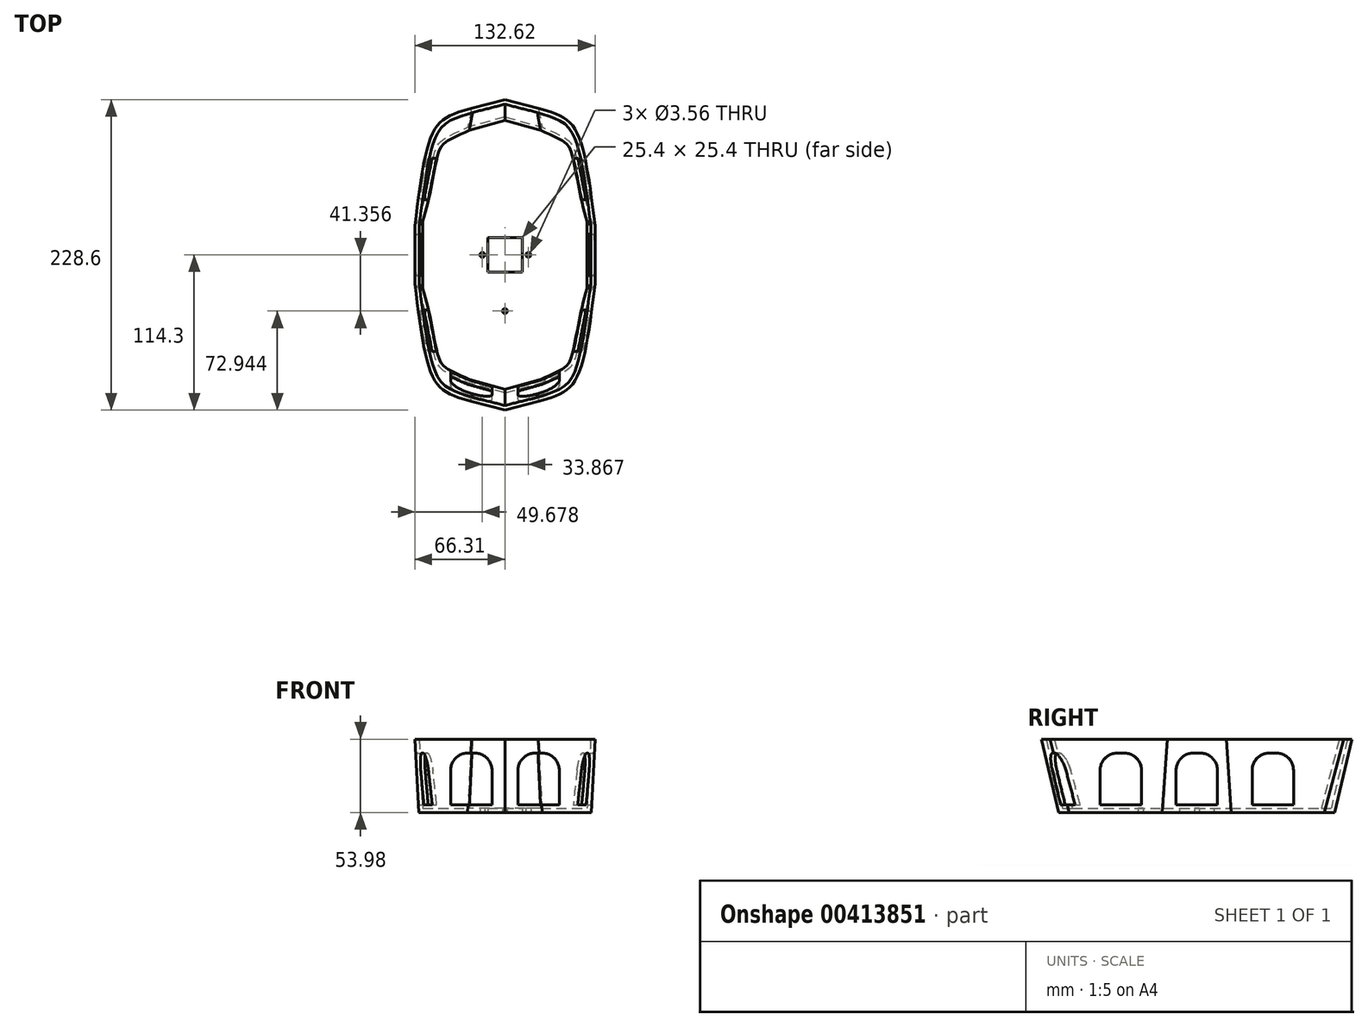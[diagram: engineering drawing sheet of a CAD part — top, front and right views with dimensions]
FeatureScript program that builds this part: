
annotation { "Feature Type Name" : "Feature", "Feature Type Description" : "" }
export const myFeature = defineFeature(function(context is Context, id is Id, definition is map)
    precondition{}
    {
        {
            var Q0;
            Q0=qCreatedBy(makeId("Top.planeOp"),FACE);
            var sketch = newSketch(context, id + "F0", { "sketchPlane" : qUnion([Q0])});
            skLineSegment(sketch, "E0", {"start": v(-63.5, 0) * mm, "end": v(-63.5, -25.4) * mm});
            skLineSegment(sketch, "E1", {"start": v(0, -101.6) * mm, "end": v(-27.43, -93.95) * mm});
            skFitSpline(sketch, "E2", {"points": [v(-63.5, -25.4) * mm, v(-51.66, -76.12) * mm, v(-27.43, -93.95) * mm], "startDerivative": vector(34.98, -106.28) * mm, "endDerivative": vector(126.69, -55.22) * mm});
            skFitSpline(sketch, "E3.MirrorCS", {"points": [v(-63.5, 25.4) * mm, v(-51.66, 76.12) * mm, v(-27.43, 93.95) * mm], "startDerivative": vector(34.98, 106.28) * mm, "endDerivative": vector(126.69, 55.22) * mm});
            skLineSegment(sketch, "E4.MirrorCS", {"start": v(0, 101.6) * mm, "end": v(-27.43, 93.95) * mm});
            skLineSegment(sketch, "E5.MirrorCS", {"start": v(-63.5, 0) * mm, "end": v(-63.5, 25.4) * mm});
            skLineSegment(sketch, "E6.MirrorCS", {"start": v(0, -101.6) * mm, "end": v(27.43, -93.95) * mm});
            skFitSpline(sketch, "E7.MirrorCS", {"points": [v(63.5, 25.4) * mm, v(51.66, 76.12) * mm, v(27.43, 93.95) * mm], "startDerivative": vector(-34.98, 106.28) * mm, "endDerivative": vector(-126.69, 55.22) * mm});
            skLineSegment(sketch, "E8.MirrorCS", {"start": v(63.5, 0) * mm, "end": v(63.5, -25.4) * mm});
            skFitSpline(sketch, "E9.MirrorCS", {"points": [v(63.5, -25.4) * mm, v(51.66, -76.12) * mm, v(27.43, -93.95) * mm], "startDerivative": vector(-34.98, -106.28) * mm, "endDerivative": vector(-126.69, -55.22) * mm});
            skLineSegment(sketch, "E10.MirrorCS", {"start": v(0, 101.6) * mm, "end": v(27.43, 93.95) * mm});
            skLineSegment(sketch, "E11.MirrorCS", {"start": v(63.5, 0) * mm, "end": v(63.5, 25.4) * mm});
            skLineSegment(sketch, "E12", {"start": v(63.5, 0) * mm, "end": v(-63.5, 0) * mm});
            skLineSegment(sketch, "E13", {"start": v(0, 101.6) * mm, "end": v(0, -101.6) * mm});
            skSolve(sketch);
        }
        {
            var Q0;
            Q0=qCreatedBy(makeId("Top.planeOp"),FACE);
            cPlane(context, id + "F1", {"entities" : qUnion([Q0]), "cplaneType" : CPlaneType.OFFSET, "offset" : 25.4 * mm, "oppositeDirection" : true, "width" : 152.4 * mm, "height" : 152.4 * mm});
        }
        {
            var Q0;
            Q0=qCreatedBy(makeId("Top.planeOp"),FACE);
            cPlane(context, id + "F2", {"entities" : qUnion([Q0]), "cplaneType" : CPlaneType.OFFSET, "offset" : 53.97 * mm, "width" : 152.4 * mm, "height" : 152.4 * mm});
        }
        {
            var Q0;
            Q0=qCreatedBy(id+"F2.planeOp",FACE);
            var sketch = newSketch(context, id + "F3", { "sketchPlane" : qUnion([Q0])});
            skLineSegment(sketch, "E14", {"start": v(0, 0) * mm, "end": v(0, -114.3) * mm});
            skLineSegment(sketch, "E15", {"start": v(0, 0) * mm, "end": v(66.31, 0) * mm});
            skLineSegment(sketch, "E16", {"start": v(66.31, 0) * mm, "end": v(66.31, -21.67) * mm});
            skLineSegment(sketch, "E17", {"start": v(0, -114.3) * mm, "end": v(24.62, -108.08) * mm});
            skFitSpline(sketch, "E18", {"points": [v(24.62, -108.08) * mm, v(43.46, -100.81) * mm, v(54.7, -86.27) * mm, v(66.31, -21.67) * mm], "startDerivative": vector(76.94, 22.9) * mm, "endDerivative": vector(19.57, 158.53) * mm});
            skLineSegment(sketch, "E19.MirrorCS", {"start": v(66.31, 0) * mm, "end": v(66.31, 21.67) * mm});
            skFitSpline(sketch, "E20.MirrorCS", {"points": [v(24.62, 108.08) * mm, v(43.46, 100.81) * mm, v(54.7, 86.27) * mm, v(66.31, 21.67) * mm], "startDerivative": vector(76.94, -22.9) * mm, "endDerivative": vector(19.57, -158.53) * mm});
            skLineSegment(sketch, "E21.MirrorCS", {"start": v(0, 114.3) * mm, "end": v(24.62, 108.08) * mm});
            skLineSegment(sketch, "E22.MirrorCS", {"start": v(0, 114.3) * mm, "end": v(-24.62, 108.08) * mm});
            skFitSpline(sketch, "E23.MirrorCS", {"points": [v(-24.62, 108.08) * mm, v(-43.46, 100.81) * mm, v(-54.7, 86.27) * mm, v(-66.31, 21.67) * mm], "startDerivative": vector(-76.94, -22.9) * mm, "endDerivative": vector(-19.57, -158.53) * mm});
            skLineSegment(sketch, "E24.MirrorCS", {"start": v(-66.31, 0) * mm, "end": v(-66.31, 21.67) * mm});
            skLineSegment(sketch, "E25.MirrorCS", {"start": v(-66.31, 0) * mm, "end": v(-66.31, -21.67) * mm});
            skFitSpline(sketch, "E26.MirrorCS", {"points": [v(-24.62, -108.08) * mm, v(-43.46, -100.81) * mm, v(-54.7, -86.27) * mm, v(-66.31, -21.67) * mm], "startDerivative": vector(-76.94, 22.9) * mm, "endDerivative": vector(-19.57, 158.53) * mm});
            skLineSegment(sketch, "E27.MirrorCS", {"start": v(0, -114.3) * mm, "end": v(-24.62, -108.08) * mm});
            skLineSegment(sketch, "E28", {"start": v(0, 114.3) * mm, "end": v(0, 0) * mm});
            skLineSegment(sketch, "E29", {"start": v(-66.31, 0) * mm, "end": v(0, 0) * mm});
            skSolve(sketch);
        }
        {
            var Q0;
            Q0=makeQuery(id+"F3.imprint","IMPRINT",FACE,{"disambiguationData":[TD([[makeQuery(id+"F3.imprint","IMPRINT",EDGE,{"derivedFrom":sQuery(id+"F3.wireOp",EDGE,"E22.MirrorCS")}),1.0]])]});
            var Q1;
            Q1=makeQuery(id+"F0.imprint","IMPRINT",FACE,{"disambiguationData":[TD([[makeQuery(id+"F0.imprint","IMPRINT",EDGE,{"derivedFrom":sQuery(id+"F0.wireOp",EDGE,"E3.MirrorCS")}),-1.0]])]});
            loft(context, id + "F4", {"sheetProfilesArray" : [{ "sheetProfileEntities" : qUnion([Q0]) }, { "sheetProfileEntities" : qUnion([Q1]) }]});
        }
        {
            var Q1;
            Q1=makeQuery(id+"F3.imprint","IMPRINT",FACE,{"disambiguationData":[TD([[makeQuery(id+"F3.imprint","IMPRINT",EDGE,{"derivedFrom":sQuery(id+"F3.wireOp",EDGE,"E14")}),-1.0]])]});
            var Q2;
            {var subQ1=sQuery(id+"F0.wireOp",EDGE,"E0");Q2=makeQuery(id+"F0.imprint","IMPRINT",FACE,{"disambiguationData":[TD([[makeQuery(id+"F0.imprint","IMPRINT",EDGE,{"derivedFrom":subQ1}),1.0]])]});}
            loft(context, id + "F5", {"operationType" : NewBodyOperationType.ADD, "sheetProfilesArray" : [{ "sheetProfileEntities" : qUnion([Q1]) }, { "sheetProfileEntities" : qUnion([Q2]) }]});
        }
        {
            var Q1;
            Q1=makeQuery(id+"F3.imprint","IMPRINT",FACE,{"disambiguationData":[TD([[makeQuery(id+"F3.imprint","IMPRINT",EDGE,{"derivedFrom":sQuery(id+"F3.wireOp",EDGE,"E14")}),1.0]])]});
            var Q2;
            {var subQ4=sQuery(id+"F0.wireOp",EDGE,"E6.MirrorCS");Q2=makeQuery(id+"F0.imprint","IMPRINT",FACE,{"disambiguationData":[TD([[makeQuery(id+"F0.imprint","IMPRINT",EDGE,{"derivedFrom":subQ4}),1.0]])]});}
            loft(context, id + "F6", {"operationType" : NewBodyOperationType.ADD, "sheetProfilesArray" : [{ "sheetProfileEntities" : qUnion([Q1]) }, { "sheetProfileEntities" : qUnion([Q2]) }]});
        }
        {
            var Q1;
            Q1=makeQuery(id+"F3.imprint","IMPRINT",FACE,{"disambiguationData":[TD([[makeQuery(id+"F3.imprint","IMPRINT",EDGE,{"derivedFrom":sQuery(id+"F3.wireOp",EDGE,"E15")}),1.0]])]});
            var Q2;
            Q2=makeQuery(id+"F0.imprint","IMPRINT",FACE,{"disambiguationData":[TD([[makeQuery(id+"F0.imprint","IMPRINT",EDGE,{"derivedFrom":sQuery(id+"F0.wireOp",EDGE,"E7.MirrorCS")}),1.0]])]});
            loft(context, id + "F7", {"operationType" : NewBodyOperationType.ADD, "sheetProfilesArray" : [{ "sheetProfileEntities" : qUnion([Q1]) }, { "sheetProfileEntities" : qUnion([Q2]) }]});
        }
        {
            var Q0;
            {var subQ0=makeQuery(id+"F3.imprint","IMPRINT",EDGE,{"derivedFrom":sQuery(id+"F3.wireOp",EDGE,"E15")});var subQ2=makeQuery(id+"F3.imprint","IMPRINT",EDGE,{"derivedFrom":sQuery(id+"F3.wireOp",EDGE,"E14")});Q0=makeQuery(id+"F7.boolean.opBoolean","MERGE",FACE,{"derivedFrom":[makeQuery(id+"F6.boolean.opBoolean","MERGE",FACE,{"derivedFrom":[makeQuery(id+"F5.boolean.opBoolean","MERGE",FACE,{"derivedFrom":[makeQuery(id+"F4.opLoft","CAP_FACE",FACE,{"disambiguationData":[OSD([makeQuery(id+"F3.imprint","IMPRINT",FACE,{"disambiguationData":[TD([[makeQuery(id+"F3.imprint","IMPRINT",EDGE,{"derivedFrom":sQuery(id+"F3.wireOp",EDGE,"E22.MirrorCS")}),1.0]])]})])],"isStart":true}),makeQuery(id+"F5.opLoft","CAP_FACE",FACE,{"disambiguationData":[OSD([makeQuery(id+"F3.imprint","IMPRINT",FACE,{"disambiguationData":[TD([[subQ2,-1.0]])]})])],"isStart":true})]}),makeQuery(id+"F6.opLoft","CAP_FACE",FACE,{"disambiguationData":[OSD([makeQuery(id+"F3.imprint","IMPRINT",FACE,{"disambiguationData":[TD([[subQ2,1.0]])]})])],"isStart":true})]}),makeQuery(id+"F7.opLoft","CAP_FACE",FACE,{"disambiguationData":[OSD([makeQuery(id+"F3.imprint","IMPRINT",FACE,{"disambiguationData":[TD([[subQ0,1.0]])]})])],"isStart":true})]});}
            shell(context, id + "F8", {"entities" : qUnion([Q0]), "thickness" : 3.17 * mm});
        }
        {
            var Q0;
            Q0=qCreatedBy(id+"F1.planeOp",FACE);
            var sketch = newSketch(context, id + "F9", { "sketchPlane" : qUnion([Q0])});
            skCircle(sketch, "E30", {"center": v(0, -41.36) * mm, "radius": 1.78 * mm});
            skLineSegment(sketch, "E31", {"start": v(4.75, -3.25) * mm, "end": v(-5.02, -3.25) * mm});
            skCircle(sketch, "E32.MirrorC", {"center": v(0, 41.36) * mm, "radius": 1.78 * mm});
            skLineSegment(sketch, "E33.bottom", {"start": v(-12.7, -12.7) * mm, "end": v(12.7, -12.7) * mm});
            skLineSegment(sketch, "E33.top", {"start": v(-12.7, 12.7) * mm, "end": v(12.7, 12.7) * mm});
            skLineSegment(sketch, "E33.left", {"start": v(-12.7, -12.7) * mm, "end": v(-12.7, 12.7) * mm});
            skLineSegment(sketch, "E33.right", {"start": v(12.7, -12.7) * mm, "end": v(12.7, 12.7) * mm});
            skLineSegment(sketch, "E34", {"start": v(0, -41.36) * mm, "end": v(0, 41.36) * mm});
            skCircle(sketch, "E35", {"center": v(-16.63, 0) * mm, "radius": 1.78 * mm});
            skCircle(sketch, "E36", {"center": v(17.23, 0) * mm, "radius": 1.78 * mm});
            skSolve(sketch);
        }
        {
            var Q0;
            Q0=makeQuery(id+"F9.imprint","IMPRINT",FACE,{"disambiguationData":[TD([[makeQuery(id+"F9.imprint","IMPRINT",EDGE,{"derivedFrom":sQuery(id+"F9.wireOp",EDGE,"E33.bottom")}),1.0]])]});
            var Q1;
            Q1=makeQuery(id+"F9.imprint","IMPRINT",FACE,{"disambiguationData":[TD([[makeQuery(id+"F9.imprint","IMPRINT",EDGE,{"derivedFrom":sQuery(id+"F9.wireOp",EDGE,"E30")}),1.0]])]});
            var Q2;
            Q2=makeQuery(id+"F9.imprint","IMPRINT",FACE,{"disambiguationData":[TD([[makeQuery(id+"F9.imprint","IMPRINT",EDGE,{"derivedFrom":sQuery(id+"F9.wireOp",EDGE,"E32.MirrorC")}),-1.0]])]});
            var Q3;
            Q3=makeQuery(id+"F9.imprint","IMPRINT",FACE,{"disambiguationData":[TD([[makeQuery(id+"F9.imprint","IMPRINT",EDGE,{"derivedFrom":sQuery(id+"F9.wireOp",EDGE,"E36")}),1.0]])]});
            var Q4;
            Q4=makeQuery(id+"F9.imprint","IMPRINT",FACE,{"disambiguationData":[TD([[makeQuery(id+"F9.imprint","IMPRINT",EDGE,{"derivedFrom":sQuery(id+"F9.wireOp",EDGE,"E35")}),1.0]])]});
            var Q5;
            {var subQ9=sQuery(id+"F0.wireOp",EDGE,"E6.MirrorCS");var subQ13=sQuery(id+"F0.wireOp",EDGE,"E0");Q5=makeQuery(id+"F8.opShell","OFFSET_FACE",FACE,{"disambiguationData":[OSD([makeQuery(id+"F0.imprint","IMPRINT",FACE,{"disambiguationData":[TD([[makeQuery(id+"F0.imprint","IMPRINT",EDGE,{"derivedFrom":subQ13}),1.0]])]}),makeQuery(id+"F0.imprint","IMPRINT",FACE,{"disambiguationData":[TD([[makeQuery(id+"F0.imprint","IMPRINT",EDGE,{"derivedFrom":sQuery(id+"F0.wireOp",EDGE,"E3.MirrorCS")}),-1.0]])]}),makeQuery(id+"F0.imprint","IMPRINT",FACE,{"disambiguationData":[TD([[makeQuery(id+"F0.imprint","IMPRINT",EDGE,{"derivedFrom":subQ9}),1.0]])]}),makeQuery(id+"F0.imprint","IMPRINT",FACE,{"disambiguationData":[TD([[makeQuery(id+"F0.imprint","IMPRINT",EDGE,{"derivedFrom":sQuery(id+"F0.wireOp",EDGE,"E7.MirrorCS")}),1.0]])]})])]});}
            extrude(context, id + "F10", {"entities" : qUnion([Q0, Q1, Q2, Q3, Q4]), "operationType" : NewBodyOperationType.REMOVE, "endBound" : BoundingType.UP_TO_SURFACE, "endBoundEntityFace" : qUnion([Q5]), "depth" : 25.4 * mm});
        }
        {
            var Q0;
            Q0=qCreatedBy(makeId("Front.planeOp"),FACE);
            var sketch = newSketch(context, id + "F11", { "sketchPlane" : qUnion([Q0])});
            skLineSegment(sketch, "E37", {"start": v(-40.03, 5.72) * mm, "end": v(-9.55, 5.72) * mm});
            skLineSegment(sketch, "E38", {"start": v(-9.55, 43.81) * mm, "end": v(-40.03, 43.81) * mm});
            skLineSegment(sketch, "E39", {"start": v(-40.03, 43.81) * mm, "end": v(-40.03, 5.72) * mm});
            skLineSegment(sketch, "E40.MirrorCS", {"start": v(40.03, 5.72) * mm, "end": v(9.55, 5.72) * mm});
            skLineSegment(sketch, "E41.MirrorCS", {"start": v(9.55, 43.81) * mm, "end": v(40.03, 43.81) * mm});
            skLineSegment(sketch, "E42.MirrorCS", {"start": v(40.03, 43.81) * mm, "end": v(40.03, 5.72) * mm});
            skLineSegment(sketch, "E43", {"start": v(-9.55, 5.72) * mm, "end": v(-9.55, 43.81) * mm});
            skLineSegment(sketch, "E44", {"start": v(9.55, 5.72) * mm, "end": v(9.55, 43.81) * mm});
            skSolve(sketch);
        }
        {
            var Q0;
            Q0 = qSketchRegion(id + "F11", true);
            extrude(context, id + "F12", {"entities" : qUnion([Q0]), "operationType" : NewBodyOperationType.REMOVE, "depth" : 179.07 * mm});
        }
        {
            var Q0;
            Q0=makeQuery(id+"F12.boolean.opBoolean","COPY",EDGE,{"derivedFrom":makeQuery(id+"F12.opExtrude","SWEPT_EDGE",EDGE,{"disambiguationData":[OSD([sQuery(id+"F11.wireOp",EDGE,"E38"),sQuery(id+"F11.wireOp",EDGE,"E43")])]})});
            var Q1;
            Q1=makeQuery(id+"F12.boolean.opBoolean","COPY",EDGE,{"derivedFrom":makeQuery(id+"F12.opExtrude","SWEPT_EDGE",EDGE,{"disambiguationData":[OSD([sQuery(id+"F11.wireOp",EDGE,"E38"),sQuery(id+"F11.wireOp",EDGE,"E39")])]})});
            var Q2;
            Q2=makeQuery(id+"F12.boolean.opBoolean","COPY",EDGE,{"derivedFrom":makeQuery(id+"F12.opExtrude","SWEPT_EDGE",EDGE,{"disambiguationData":[OSD([sQuery(id+"F11.wireOp",EDGE,"E41.MirrorCS"),sQuery(id+"F11.wireOp",EDGE,"E44")])]})});
            var Q3;
            Q3=makeQuery(id+"F12.boolean.opBoolean","COPY",EDGE,{"derivedFrom":makeQuery(id+"F12.opExtrude","SWEPT_EDGE",EDGE,{"disambiguationData":[OSD([sQuery(id+"F11.wireOp",EDGE,"E41.MirrorCS"),sQuery(id+"F11.wireOp",EDGE,"E42.MirrorCS")])]})});
            fillet(context, id + "F13", {"entities" : qUnion([Q0, Q1, Q2, Q3]), "radius" : 12.7 * mm, "tangentPropagation" : true, "allowEdgeOverflow" : false});
        }
        {
            var Q0;
            Q0=qCreatedBy(makeId("Right.planeOp"),FACE);
            var sketch = newSketch(context, id + "F14", { "sketchPlane" : qUnion([Q0])});
            skLineSegment(sketch, "E45", {"start": v(0, 0) * mm, "end": v(-15.24, 0) * mm});
            skLineSegment(sketch, "E46", {"start": v(-15.24, 0) * mm, "end": v(-15.24, 5.71) * mm});
            skLineSegment(sketch, "E47", {"start": v(-15.24, 5.71) * mm, "end": v(15.24, 5.71) * mm});
            skLineSegment(sketch, "E48", {"start": v(15.24, 5.71) * mm, "end": v(15.24, 43.81) * mm});
            skLineSegment(sketch, "E49", {"start": v(15.24, 43.81) * mm, "end": v(-15.24, 43.81) * mm});
            skLineSegment(sketch, "E50", {"start": v(-15.24, 43.81) * mm, "end": v(-15.24, 5.71) * mm});
            skLineSegment(sketch, "E51", {"start": v(-55.97, 0) * mm, "end": v(-71.2, 0) * mm});
            skLineSegment(sketch, "E52", {"start": v(-71.2, 0) * mm, "end": v(-71.2, 5.71) * mm});
            skLineSegment(sketch, "E53", {"start": v(-71.2, 5.71) * mm, "end": v(-40.73, 5.71) * mm});
            skLineSegment(sketch, "E54", {"start": v(-40.73, 5.71) * mm, "end": v(-40.73, 43.82) * mm});
            skLineSegment(sketch, "E55", {"start": v(-40.73, 43.82) * mm, "end": v(-71.2, 43.82) * mm});
            skLineSegment(sketch, "E56", {"start": v(-71.2, 43.81) * mm, "end": v(-71.2, 5.71) * mm});
            skLineSegment(sketch, "E57", {"start": v(0, 0) * mm, "end": v(0, -30.53) * mm});
            skLineSegment(sketch, "E58.MirrorCS", {"start": v(71.2, 0) * mm, "end": v(71.2, 5.71) * mm});
            skLineSegment(sketch, "E59.MirrorCS", {"start": v(71.2, 43.81) * mm, "end": v(71.2, 5.71) * mm});
            skLineSegment(sketch, "E60.MirrorCS", {"start": v(40.73, 43.82) * mm, "end": v(71.2, 43.82) * mm});
            skLineSegment(sketch, "E61.MirrorCS", {"start": v(40.73, 5.71) * mm, "end": v(40.73, 43.82) * mm});
            skLineSegment(sketch, "E62.MirrorCS", {"start": v(55.97, 0) * mm, "end": v(71.2, 0) * mm});
            skLineSegment(sketch, "E63.MirrorCS", {"start": v(71.2, 5.71) * mm, "end": v(40.73, 5.71) * mm});
            skSolve(sketch);
        }
        {
            var Q0;
            Q0 = qSketchRegion(id + "F14", true);
            extrude(context, id + "F15", {"entities" : qUnion([Q0]), "operationType" : NewBodyOperationType.REMOVE, "oppositeDirection" : true, "depth" : 119.13 * mm, "hasSecondDirection" : true, "secondDirectionOppositeDirection" : false, "secondDirectionDepth" : 125.48 * mm});
        }
        {
            var Q0;
            {var subQ0=sQuery(id+"F3.wireOp",EDGE,"E18");var subQ1=sQuery(id+"F3.wireOp",EDGE,"E17");var subQ2=sQuery(id+"F3.wireOp",EDGE,"E16");var subQ3=sQuery(id+"F0.wireOp",EDGE,"E9.MirrorCS");var subQ4=sQuery(id+"F0.wireOp",EDGE,"E8.MirrorCS");var subQ5=sQuery(id+"F0.wireOp",EDGE,"E6.MirrorCS");var subQ6=sQuery(id+"F14.wireOp",EDGE,"E54");var subQ7=sQuery(id+"F14.wireOp",EDGE,"E55");Q0=makeQuery(id+"F15.boolean.opBoolean","COPY",EDGE,{"disambiguationData":[TD([makeQuery(id+"F6.opLoft","SWEPT_FACE",FACE,{"disambiguationData":[OSD([subQ5,subQ4,subQ3,subQ2,subQ1,subQ0])]})])],"derivedFrom":makeQuery(id+"F15.opExtrude","SWEPT_EDGE",EDGE,{"disambiguationData":[OSD([subQ6,subQ7])]})});}
            var Q1;
            {var subQ0=sQuery(id+"F3.wireOp",EDGE,"E18");var subQ1=sQuery(id+"F3.wireOp",EDGE,"E17");var subQ2=sQuery(id+"F3.wireOp",EDGE,"E16");var subQ3=sQuery(id+"F0.wireOp",EDGE,"E9.MirrorCS");var subQ4=sQuery(id+"F0.wireOp",EDGE,"E8.MirrorCS");var subQ5=sQuery(id+"F0.wireOp",EDGE,"E6.MirrorCS");var subQ6=sQuery(id+"F14.wireOp",EDGE,"E56");var subQ7=sQuery(id+"F14.wireOp",EDGE,"E55");Q1=makeQuery(id+"F15.boolean.opBoolean","COPY",EDGE,{"disambiguationData":[TD([makeQuery(id+"F6.opLoft","SWEPT_FACE",FACE,{"disambiguationData":[OSD([subQ5,subQ4,subQ3,subQ2,subQ1,subQ0])]})])],"derivedFrom":makeQuery(id+"F15.opExtrude","SWEPT_EDGE",EDGE,{"disambiguationData":[OSD([subQ7,subQ6])]})});}
            var Q2;
            {var subQ0=sQuery(id+"F14.wireOp",EDGE,"E49");var subQ2=sQuery(id+"F3.wireOp",EDGE,"E19.MirrorCS");var subQ3=sQuery(id+"F3.wireOp",EDGE,"E16");var subQ4=sQuery(id+"F3.wireOp",EDGE,"E15");var subQ5=sQuery(id+"F0.wireOp",EDGE,"E12");var subQ6=sQuery(id+"F0.wireOp",EDGE,"E11.MirrorCS");var subQ7=sQuery(id+"F0.wireOp",EDGE,"E8.MirrorCS");var subQ9=sQuery(id+"F3.wireOp",EDGE,"E18");var subQ10=sQuery(id+"F0.wireOp",EDGE,"E9.MirrorCS");var subQ11=sQuery(id+"F14.wireOp",EDGE,"E50");Q2=makeQuery(id+"F15.boolean.opBoolean","COPY",EDGE,{"disambiguationData":[TD([makeQuery(id+"F6.opLoft","SWEPT_FACE",FACE,{"disambiguationData":[OSD([subQ7,subQ10,subQ6,subQ5,subQ4,subQ3,subQ9,subQ2])]})])],"derivedFrom":makeQuery(id+"F15.opExtrude","SWEPT_EDGE",EDGE,{"disambiguationData":[OSD([subQ0,subQ11])]})});}
            var Q3;
            {var subQ0=sQuery(id+"F14.wireOp",EDGE,"E48");var subQ2=sQuery(id+"F3.wireOp",EDGE,"E19.MirrorCS");var subQ3=sQuery(id+"F3.wireOp",EDGE,"E16");var subQ4=sQuery(id+"F3.wireOp",EDGE,"E15");var subQ5=sQuery(id+"F0.wireOp",EDGE,"E12");var subQ6=sQuery(id+"F0.wireOp",EDGE,"E11.MirrorCS");var subQ7=sQuery(id+"F0.wireOp",EDGE,"E8.MirrorCS");var subQ9=sQuery(id+"F3.wireOp",EDGE,"E18");var subQ10=sQuery(id+"F0.wireOp",EDGE,"E9.MirrorCS");var subQ11=sQuery(id+"F14.wireOp",EDGE,"E49");Q3=makeQuery(id+"F15.boolean.opBoolean","COPY",EDGE,{"disambiguationData":[TD([makeQuery(id+"F6.opLoft","SWEPT_FACE",FACE,{"disambiguationData":[OSD([subQ7,subQ10,subQ6,subQ5,subQ4,subQ3,subQ9,subQ2])]})])],"derivedFrom":makeQuery(id+"F15.opExtrude","SWEPT_EDGE",EDGE,{"disambiguationData":[OSD([subQ0,subQ11])]})});}
            var Q4;
            {var subQ0=sQuery(id+"F3.wireOp",EDGE,"E21.MirrorCS");var subQ1=sQuery(id+"F3.wireOp",EDGE,"E20.MirrorCS");var subQ2=sQuery(id+"F3.wireOp",EDGE,"E19.MirrorCS");var subQ3=sQuery(id+"F0.wireOp",EDGE,"E11.MirrorCS");var subQ4=sQuery(id+"F0.wireOp",EDGE,"E10.MirrorCS");var subQ5=sQuery(id+"F0.wireOp",EDGE,"E7.MirrorCS");var subQ6=sQuery(id+"F14.wireOp",EDGE,"E59.MirrorCS");var subQ7=sQuery(id+"F14.wireOp",EDGE,"E60.MirrorCS");Q4=makeQuery(id+"F15.boolean.opBoolean","COPY",EDGE,{"disambiguationData":[TD([makeQuery(id+"F7.opLoft","SWEPT_FACE",FACE,{"disambiguationData":[OSD([subQ5,subQ4,subQ3,subQ2,subQ1,subQ0])]})])],"derivedFrom":makeQuery(id+"F15.opExtrude","SWEPT_EDGE",EDGE,{"disambiguationData":[OSD([subQ6,subQ7])]})});}
            var Q5;
            {var subQ0=sQuery(id+"F3.wireOp",EDGE,"E21.MirrorCS");var subQ1=sQuery(id+"F3.wireOp",EDGE,"E20.MirrorCS");var subQ2=sQuery(id+"F3.wireOp",EDGE,"E19.MirrorCS");var subQ3=sQuery(id+"F0.wireOp",EDGE,"E11.MirrorCS");var subQ4=sQuery(id+"F0.wireOp",EDGE,"E10.MirrorCS");var subQ5=sQuery(id+"F0.wireOp",EDGE,"E7.MirrorCS");var subQ6=sQuery(id+"F14.wireOp",EDGE,"E61.MirrorCS");var subQ7=sQuery(id+"F14.wireOp",EDGE,"E60.MirrorCS");Q5=makeQuery(id+"F15.boolean.opBoolean","COPY",EDGE,{"disambiguationData":[TD([makeQuery(id+"F7.opLoft","SWEPT_FACE",FACE,{"disambiguationData":[OSD([subQ5,subQ4,subQ3,subQ2,subQ1,subQ0])]})])],"derivedFrom":makeQuery(id+"F15.opExtrude","SWEPT_EDGE",EDGE,{"disambiguationData":[OSD([subQ7,subQ6])]})});}
            var Q6;
            {var subQ0=sQuery(id+"F3.wireOp",EDGE,"E24.MirrorCS");var subQ1=sQuery(id+"F3.wireOp",EDGE,"E23.MirrorCS");var subQ2=sQuery(id+"F3.wireOp",EDGE,"E22.MirrorCS");var subQ3=sQuery(id+"F0.wireOp",EDGE,"E5.MirrorCS");var subQ4=sQuery(id+"F0.wireOp",EDGE,"E4.MirrorCS");var subQ5=sQuery(id+"F0.wireOp",EDGE,"E3.MirrorCS");var subQ6=sQuery(id+"F14.wireOp",EDGE,"E59.MirrorCS");var subQ7=sQuery(id+"F14.wireOp",EDGE,"E60.MirrorCS");Q6=makeQuery(id+"F15.boolean.opBoolean","COPY",EDGE,{"disambiguationData":[TD([makeQuery(id+"F4.opLoft","SWEPT_FACE",FACE,{"disambiguationData":[OSD([subQ5,subQ4,subQ3,subQ2,subQ1,subQ0])]})])],"derivedFrom":makeQuery(id+"F15.opExtrude","SWEPT_EDGE",EDGE,{"disambiguationData":[OSD([subQ6,subQ7])]})});}
            var Q7;
            {var subQ0=sQuery(id+"F3.wireOp",EDGE,"E24.MirrorCS");var subQ1=sQuery(id+"F3.wireOp",EDGE,"E23.MirrorCS");var subQ2=sQuery(id+"F3.wireOp",EDGE,"E22.MirrorCS");var subQ3=sQuery(id+"F0.wireOp",EDGE,"E5.MirrorCS");var subQ4=sQuery(id+"F0.wireOp",EDGE,"E4.MirrorCS");var subQ5=sQuery(id+"F0.wireOp",EDGE,"E3.MirrorCS");var subQ6=sQuery(id+"F14.wireOp",EDGE,"E60.MirrorCS");var subQ7=sQuery(id+"F14.wireOp",EDGE,"E61.MirrorCS");Q7=makeQuery(id+"F15.boolean.opBoolean","COPY",EDGE,{"disambiguationData":[TD([makeQuery(id+"F4.opLoft","SWEPT_FACE",FACE,{"disambiguationData":[OSD([subQ5,subQ4,subQ3,subQ2,subQ1,subQ0])]})])],"derivedFrom":makeQuery(id+"F15.opExtrude","SWEPT_EDGE",EDGE,{"disambiguationData":[OSD([subQ6,subQ7])]})});}
            var Q8;
            {var subQ0=sQuery(id+"F14.wireOp",EDGE,"E49");var subQ1=sQuery(id+"F3.wireOp",EDGE,"E29");var subQ3=sQuery(id+"F3.wireOp",EDGE,"E25.MirrorCS");var subQ4=sQuery(id+"F3.wireOp",EDGE,"E24.MirrorCS");var subQ5=sQuery(id+"F3.wireOp",EDGE,"E23.MirrorCS");var subQ6=sQuery(id+"F0.wireOp",EDGE,"E12");var subQ7=sQuery(id+"F0.wireOp",EDGE,"E5.MirrorCS");var subQ8=sQuery(id+"F0.wireOp",EDGE,"E3.MirrorCS");var subQ10=sQuery(id+"F0.wireOp",EDGE,"E0");var subQ11=sQuery(id+"F14.wireOp",EDGE,"E50");Q8=makeQuery(id+"F15.boolean.opBoolean","COPY",EDGE,{"disambiguationData":[TD([makeQuery(id+"F4.opLoft","SWEPT_FACE",FACE,{"disambiguationData":[OSD([subQ10,subQ8,subQ7,subQ6,subQ5,subQ4,subQ3,subQ1])]})])],"derivedFrom":makeQuery(id+"F15.opExtrude","SWEPT_EDGE",EDGE,{"disambiguationData":[OSD([subQ0,subQ11])]})});}
            var Q9;
            {var subQ0=sQuery(id+"F3.wireOp",EDGE,"E27.MirrorCS");var subQ1=sQuery(id+"F3.wireOp",EDGE,"E26.MirrorCS");var subQ2=sQuery(id+"F3.wireOp",EDGE,"E25.MirrorCS");var subQ3=sQuery(id+"F0.wireOp",EDGE,"E2");var subQ4=sQuery(id+"F0.wireOp",EDGE,"E1");var subQ5=sQuery(id+"F0.wireOp",EDGE,"E0");var subQ6=sQuery(id+"F14.wireOp",EDGE,"E55");var subQ7=sQuery(id+"F14.wireOp",EDGE,"E56");Q9=makeQuery(id+"F15.boolean.opBoolean","COPY",EDGE,{"disambiguationData":[TD([makeQuery(id+"F5.opLoft","SWEPT_FACE",FACE,{"disambiguationData":[OSD([subQ5,subQ4,subQ3,subQ2,subQ1,subQ0])]})])],"derivedFrom":makeQuery(id+"F15.opExtrude","SWEPT_EDGE",EDGE,{"disambiguationData":[OSD([subQ6,subQ7])]})});}
            var Q10;
            {var subQ0=sQuery(id+"F3.wireOp",EDGE,"E27.MirrorCS");var subQ1=sQuery(id+"F3.wireOp",EDGE,"E26.MirrorCS");var subQ2=sQuery(id+"F3.wireOp",EDGE,"E25.MirrorCS");var subQ3=sQuery(id+"F0.wireOp",EDGE,"E2");var subQ4=sQuery(id+"F0.wireOp",EDGE,"E1");var subQ5=sQuery(id+"F0.wireOp",EDGE,"E0");var subQ6=sQuery(id+"F14.wireOp",EDGE,"E54");var subQ7=sQuery(id+"F14.wireOp",EDGE,"E55");Q10=makeQuery(id+"F15.boolean.opBoolean","COPY",EDGE,{"disambiguationData":[TD([makeQuery(id+"F5.opLoft","SWEPT_FACE",FACE,{"disambiguationData":[OSD([subQ5,subQ4,subQ3,subQ2,subQ1,subQ0])]})])],"derivedFrom":makeQuery(id+"F15.opExtrude","SWEPT_EDGE",EDGE,{"disambiguationData":[OSD([subQ6,subQ7])]})});}
            var Q11;
            {var subQ0=sQuery(id+"F14.wireOp",EDGE,"E48");var subQ1=sQuery(id+"F3.wireOp",EDGE,"E29");var subQ3=sQuery(id+"F3.wireOp",EDGE,"E25.MirrorCS");var subQ4=sQuery(id+"F3.wireOp",EDGE,"E24.MirrorCS");var subQ5=sQuery(id+"F3.wireOp",EDGE,"E23.MirrorCS");var subQ6=sQuery(id+"F0.wireOp",EDGE,"E12");var subQ7=sQuery(id+"F0.wireOp",EDGE,"E5.MirrorCS");var subQ8=sQuery(id+"F0.wireOp",EDGE,"E3.MirrorCS");var subQ10=sQuery(id+"F0.wireOp",EDGE,"E0");var subQ11=sQuery(id+"F14.wireOp",EDGE,"E49");Q11=makeQuery(id+"F15.boolean.opBoolean","COPY",EDGE,{"disambiguationData":[TD([makeQuery(id+"F4.opLoft","SWEPT_FACE",FACE,{"disambiguationData":[OSD([subQ10,subQ8,subQ7,subQ6,subQ5,subQ4,subQ3,subQ1])]})])],"derivedFrom":makeQuery(id+"F15.opExtrude","SWEPT_EDGE",EDGE,{"disambiguationData":[OSD([subQ0,subQ11])]})});}
            fillet(context, id + "F16", {"entities" : qUnion([Q0, Q1, Q2, Q3, Q4, Q5, Q6, Q7, Q8, Q9, Q10, Q11]), "radius" : 12.7 * mm, "tangentPropagation" : true, "allowEdgeOverflow" : false});
        }
    });
